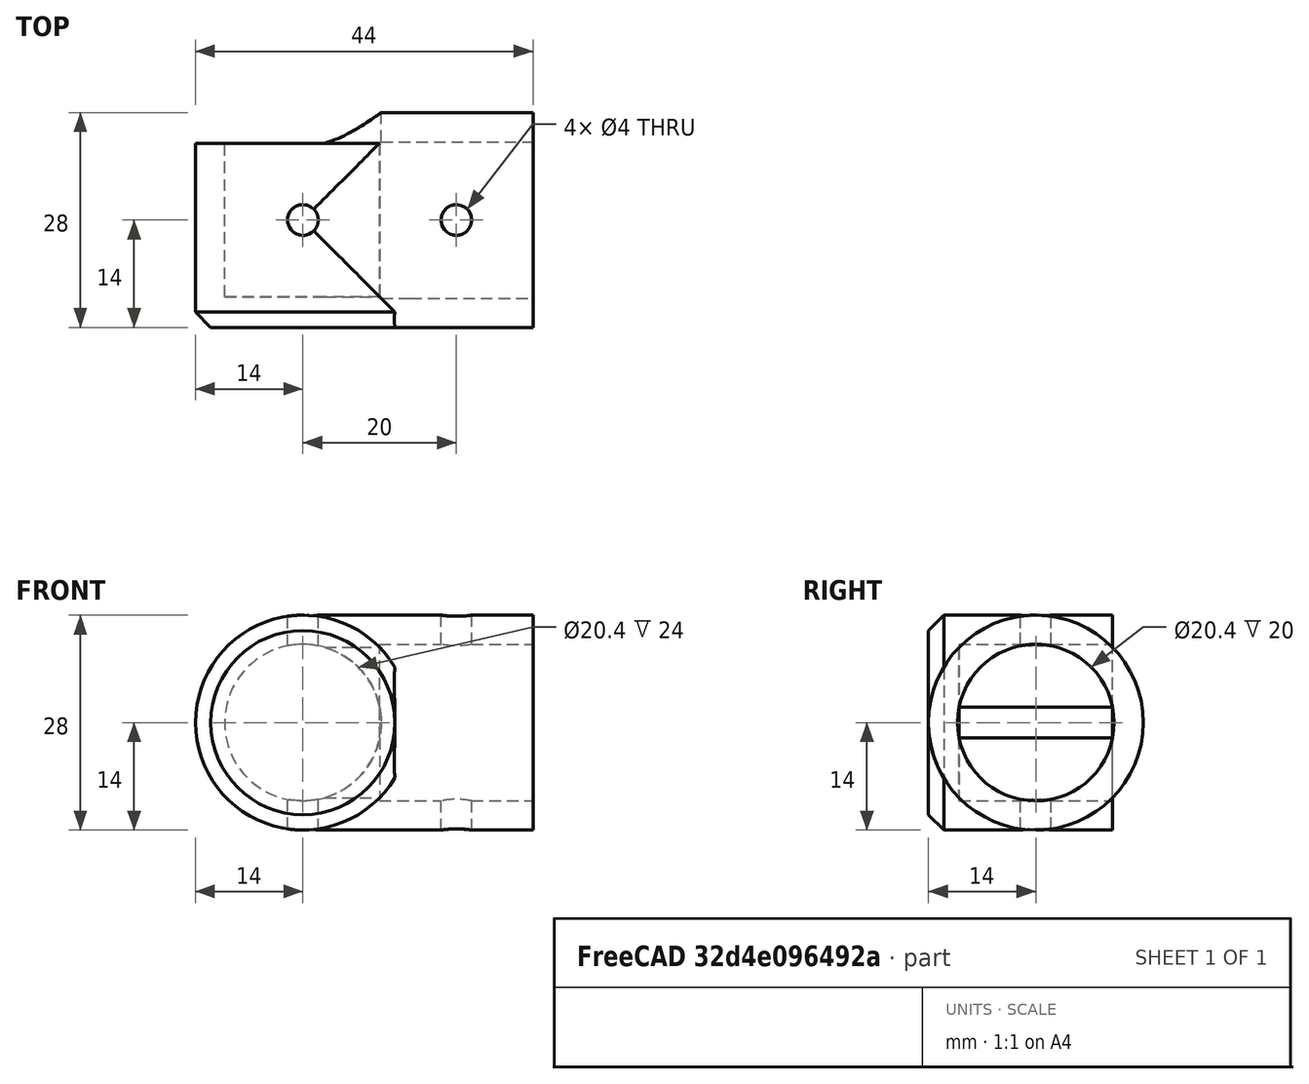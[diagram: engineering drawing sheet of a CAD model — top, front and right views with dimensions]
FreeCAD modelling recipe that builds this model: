
FCSTD DOCUMENT  (FreeCAD 0.17R13522 (Git))
Label: connector-t-cap
License: All rights reserved
LicenseURL: http://en.wikipedia.org/wiki/All_rights_reserved
objects: Part::Cylinder×7, Part::MultiFuse×3, Part::Cut×2, Part::Cone×1
note: 13 computed .brp shape members not serialized (recipe doc carries the construction recipe); baked Part::Feature solids carry a one-line shape summary decoded from their .brp

FEATURE [Part::Cylinder] Cylinder
  Angle = 360
  AttacherType = Attacher::AttachEngine3D
  Height = 30
  Placement = pos=(0,-15,0) rot=(-1,0,0;1.5708rad)
  Radius = 10.2
FEATURE [Part::Cylinder] Cylinder001
  Angle = 360
  AttacherType = Attacher::AttachEngine3D
  Height = 20
  Placement = pos=(10,0,0) rot=(0.57735,-0.57735,0.57735;4.18879rad)
  Radius = 10.2
FEATURE [Part::Cylinder] Cylinder002
  Angle = 360
  AttacherType = Attacher::AttachEngine3D
  Height = 30
  Placement = pos=(0,0,-15) rot=(0,0,1;0rad)
  Radius = 2
FEATURE [Part::Cylinder] Cylinder003
  Angle = 360
  AttacherType = Attacher::AttachEngine3D
  Height = 30
  Placement = pos=(20,0,-15) rot=(0,0,1;0rad)
  Radius = 2
FEATURE [Part::MultiFuse] Fusion  label="Negative Fusion"
  Shapes = -> [Cylinder,Cylinder001,Cylinder002,Cylinder003]
FEATURE [Part::Cylinder] Cylinder004
  Angle = 360
  AttacherType = Attacher::AttachEngine3D
  Height = 30
  Placement = pos=(0,0,0) rot=(0.57735,-0.57735,0.57735;4.18879rad)
  Radius = 14
FEATURE [Part::Cylinder] Cylinder005
  Angle = 360
  AttacherType = Attacher::AttachEngine3D
  Height = 20
  Placement = pos=(0,-10,0) rot=(-1,0,0;1.5708rad)
  Radius = 14
FEATURE [Part::MultiFuse] Fusion001
  Shapes = -> [Cylinder005,Cylinder004]
FEATURE [Part::Cut] Cut  label="Main Cut"
  Base = -> Fusion001
  Tool = -> Fusion
FEATURE [Part::Cylinder] Cylinder006
  Angle = 360
  AttacherType = Attacher::AttachEngine3D
  Height = 2
  Placement = pos=(0,-10,0) rot=(1,0,0;1.5708rad)
  Radius = 14
FEATURE [Part::Cut] Cut001  label="Cap Cut"
  Base = -> Cylinder006
  Tool = -> Cylinder001
FEATURE [Part::Cone] Cone
  Angle = 360
  AttacherType = Attacher::AttachEngine3D
  Height = 2
  Placement = pos=(0,-12,0) rot=(1,0,0;1.5708rad)
  Radius1 = 14
  Radius2 = 12
FEATURE [Part::MultiFuse] Fusion002  label="Main Fusion"
  Shapes = -> [Cut,Cut001,Cone]
